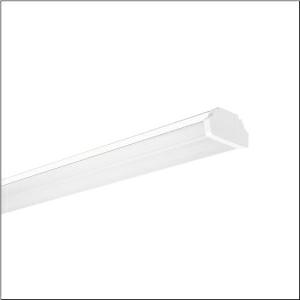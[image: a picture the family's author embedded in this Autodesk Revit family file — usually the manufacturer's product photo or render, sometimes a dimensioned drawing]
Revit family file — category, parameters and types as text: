
# Revit family: dus_r__31_mo_53bd812c1v4075_b8a3
name_source: partatom
category: Lighting Fixtures
units: mm (PartAtom-declared; Revit-internal decimal feet)

## family parameters
Cut with Voids When Loaded = No
Host = Face
Light Source = No
Part Type = Normal
Room Calculation Point = No
Round Connector Dimension = Use Diameter
Shared = No

## types (1)
- --- (1 x LED, 7620 lm, 48.9 W, 4000K)
    Apparent Load = 49 VA
    CIE Flux Codes = 47 80 95 92 100
    Color Rendering = 80
    Color Temperature = 4000K
    Default Elevation = 1800 mm
    Description = DUS® 31 MO, luminaire insert, of sheet steel, coil coated, white, length: 1.535mm, width: 81mm, height: 90mm, 5x system unit, system units: 307mm, LED rated luminous flux: 7.620lm, light colour: 840, control gear: ON/OFF Multilumen, CLOi, control gear: ECG Multilumen, with plug, 3-pole, with phase selection, mains connection: 220..240V, AC, 50/60Hz, start of lifetime: 49W, end of service life: 56W, through-wiring accessed according to module size, primary optical cover: cover, of PMMA, light emission: direct distribution, primary light characteristic: symmetric, protection rating (complete): IP20, protection rating (LED compartment): IP50, insulation class (complete): insulation class I (protective earthing), certification: CE, ENEC, VDE, UKCA, impact resistance: IK03, permissible ambient temperature for indoor applications: -35..+30°C, corresponds to IFS (International Featured Standards) requirements for safety and quality in the food industry, reducing of maximum allowable ambient temperature of 5°C with ceiling mounting, packaging unit: 1 piece
    Height = 95 mm
    Lamp = 1 x LED
    Lamp Light Flux = 7620 lm
    Lamp Power = 48.9 W
    Lamp count = 1
    Length = 1535 mm
    Luminous efficacy = 156 lm/W
    Manufacturer = Siteco
    ModVariant = No
    Model = 53BD812C1V4075
    Mounting Place = Ceiling
    Mounting Type = Pendant
    Number of Poles = 1
    OnlyDefault = Yes
    Power Factor = 1
    Product Name = DUS® 31 MO
    Product group = luminaire insert
    ProductGroupID = 901
    Protection Class = Protection class I
    Protection Degree = IP 20
    RLX_Detail_Level = 1
    RLX_Emergency_Light_Flux = 0 lm
    RLX_Emergency_Type = 0
    RLX_Emergency_Type_DB = No
    RlxData = <blob elided: 39845 chars, md5=91b61d74>
    Socket = socket
    Standby Power = 0 W
    System Light Flux = 7620 lm
    System Power = 49 W
    Type Comments = factory setting: luminous flux: 100 % | (A | C | E) | 107 mA
    Type Image = l_1319596.jpg
    URL = http://relux.com
    VarID = @adj_172659
    Voltage = 0 V
    Weight = 0.00 kg
    Width = 81 mm

## geometry (parser evidence)
native form markers: Blend x4, Sweep x12
no freeform markers — native parametric forms only
